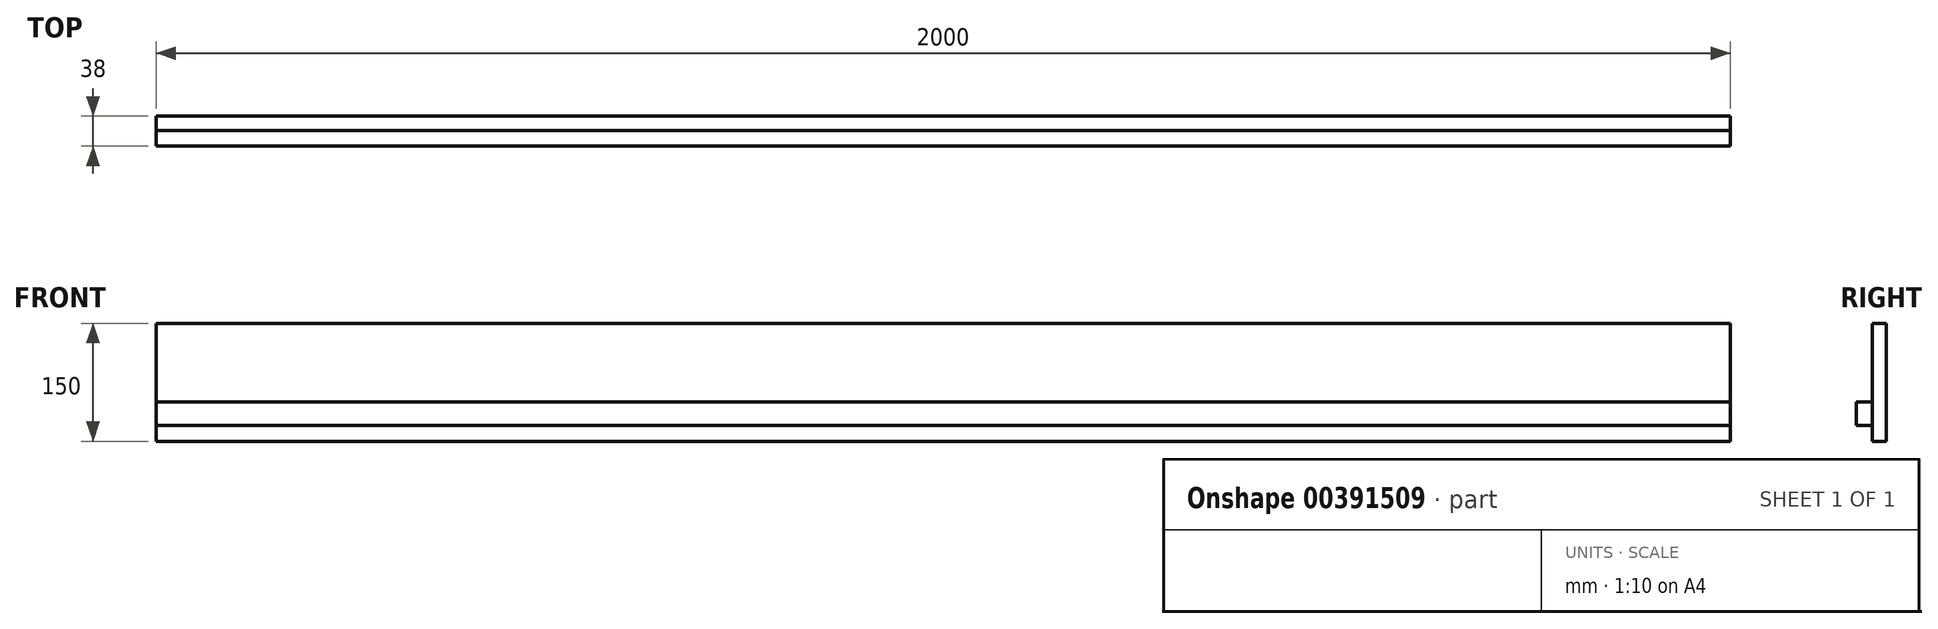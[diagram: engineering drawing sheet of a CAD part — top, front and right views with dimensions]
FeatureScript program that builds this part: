
annotation { "Feature Type Name" : "Feature", "Feature Type Description" : "" }
export const myFeature = defineFeature(function(context is Context, id is Id, definition is map)
    precondition{}
    {
        {
            var Q0;
            Q0=qCreatedBy(makeId("Front.planeOp"),FACE);
            var sketch = newSketch(context, id + "F0", { "sketchPlane" : qUnion([Q0])});
            skLineSegment(sketch, "E0.bottom", {"start": v(-1000, 150) * mm, "end": v(1000, 150) * mm});
            skLineSegment(sketch, "E0.top", {"start": v(-1000, 0) * mm, "end": v(1000, 0) * mm});
            skLineSegment(sketch, "E0.left", {"start": v(-1000, 150) * mm, "end": v(-1000, 0) * mm});
            skLineSegment(sketch, "E0.right", {"start": v(1000, 150) * mm, "end": v(1000, 0) * mm});
            skSolve(sketch);
        }
        {
            var Q0;
            Q0=makeQuery(id+"F0.imprint","IMPRINT",FACE,{"disambiguationData":[TD([[makeQuery(id+"F0.imprint","IMPRINT",EDGE,{"derivedFrom":sQuery(id+"F0.wireOp",EDGE,"E0.bottom")}),-1.0]])]});
            extrude(context, id + "F1", {"entities" : qUnion([Q0]), "oppositeDirection" : true, "depth" : 18 * mm});
        }
        {
            var Q0;
            Q0=qCreatedBy(makeId("Right.planeOp"),FACE);
            var sketch = newSketch(context, id + "F2", { "sketchPlane" : qUnion([Q0])});
            skLineSegment(sketch, "E1.bottom", {"start": v(0, 50) * mm, "end": v(-20, 50) * mm});
            skLineSegment(sketch, "E1.top", {"start": v(0, 20) * mm, "end": v(-20, 20) * mm});
            skLineSegment(sketch, "E1.left", {"start": v(0, 50) * mm, "end": v(0, 20) * mm});
            skLineSegment(sketch, "E1.right", {"start": v(-20, 50) * mm, "end": v(-20, 20) * mm});
            skSolve(sketch);
        }
        {
            var Q0;
            Q0 = qSketchRegion(id + "F2", true);
            extrude(context, id + "F3", {"entities" : qUnion([Q0]), "endBound" : BoundingType.SYMMETRIC, "depth" : 2000 * mm});
        }
    });
